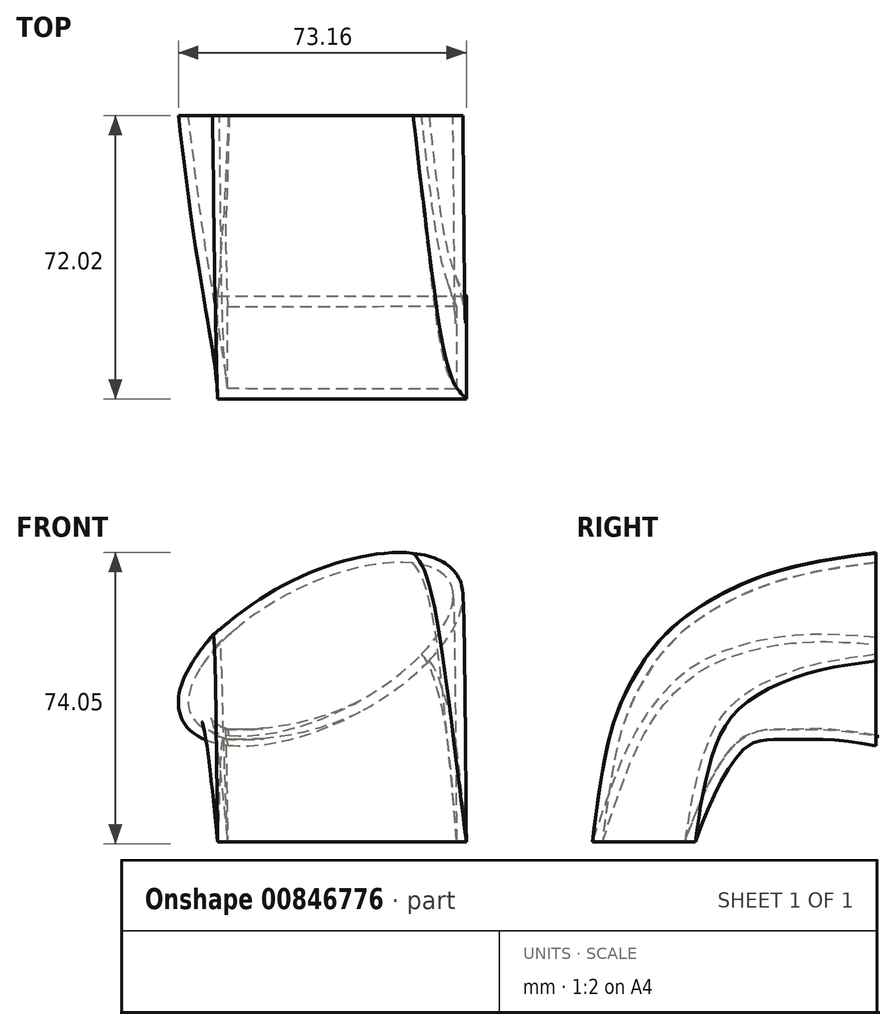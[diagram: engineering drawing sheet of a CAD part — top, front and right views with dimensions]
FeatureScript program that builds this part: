
annotation { "Feature Type Name" : "Feature", "Feature Type Description" : "" }
export const myFeature = defineFeature(function(context is Context, id is Id, definition is map)
    precondition{}
    {
        {
            var Q0;
            Q0=qCreatedBy(makeId("Front.planeOp"),FACE);
            var sketch = newSketch(context, id + "F0", { "sketchPlane" : qUnion([Q0])});
            skEllipse(sketch, "E0", {"center": v(10.24, 48.9) * mm, "majorRadius": 39.48 * mm, "minorRadius": 18.75 * mm, "majorAxis": v(0.89, 0.46)});
            skSolve(sketch);
        }
        {
            var Q0;
            Q0=qCreatedBy(makeId("Top.planeOp"),FACE);
            var sketch = newSketch(context, id + "F1", { "sketchPlane" : qUnion([Q0])});
            skLineSegment(sketch, "E1.bottom", {"start": v(-15.92, -72.02) * mm, "end": v(47.26, -72.02) * mm});
            skLineSegment(sketch, "E1.top", {"start": v(-15.92, -45.87) * mm, "end": v(47.26, -45.87) * mm});
            skLineSegment(sketch, "E1.left", {"start": v(-15.92, -72.02) * mm, "end": v(-15.92, -45.87) * mm});
            skLineSegment(sketch, "E1.right", {"start": v(47.26, -72.02) * mm, "end": v(47.26, -45.87) * mm});
            skSolve(sketch);
        }
        {
            var Q0;
            Q0=qCreatedBy(makeId("Right.planeOp"),FACE);
            var sketch = newSketch(context, id + "F2", { "sketchPlane" : qUnion([Q0])});
            skFitSpline(sketch, "E2", {"points": [v(0, 64.7) * mm, v(-52.1, 48.06) * mm, v(-72.02, 0) * mm], "startDerivative": vector(-116.53, -0.97) * mm, "endDerivative": vector(-23.25, -117.25) * mm});
            skSolve(sketch);
        }
        {
            var Q0;
            Q0=sQuery(id+"F2.wireOp",EDGE,"E2");
            var Q1;
            Q1=makeQuery(id+"F0.imprint","IMPRINT",FACE,{"disambiguationData":[TD([[makeQuery(id+"F0.imprint","IMPRINT",EDGE,{"derivedFrom":sQuery(id+"F0.wireOp",EDGE,"E0")}),1.0]])]});
            var Q2;
            Q2=makeQuery(id+"F1.imprint","IMPRINT",FACE,{"disambiguationData":[TD([[makeQuery(id+"F1.imprint","IMPRINT",EDGE,{"derivedFrom":sQuery(id+"F1.wireOp",EDGE,"E1.bottom")}),1.0]])]});
            loft(context, id + "F3", {"addSections" : true, "spine" : qUnion([Q0]), "sectionCount" : 5, "sheetProfilesArray" : [{ "sheetProfileEntities" : qUnion([Q1]) }, { "sheetProfileEntities" : qUnion([Q2]) }]});
        }
        {
            var Q0;
            Q0=makeQuery(id+"F3.opLoft","CAP_FACE",FACE,{"disambiguationData":[OSD([makeQuery(id+"F1.imprint","IMPRINT",FACE,{"disambiguationData":[TD([[makeQuery(id+"F1.imprint","IMPRINT",EDGE,{"derivedFrom":sQuery(id+"F1.wireOp",EDGE,"E1.bottom")}),1.0]])]})])],"isStart":true});
            var Q1;
            Q1=makeQuery(id+"F3.opLoft","CAP_FACE",FACE,{"disambiguationData":[OSD([makeQuery(id+"F0.imprint","IMPRINT",FACE,{"disambiguationData":[TD([[makeQuery(id+"F0.imprint","IMPRINT",EDGE,{"derivedFrom":sQuery(id+"F0.wireOp",EDGE,"E0")}),1.0]])]})])],"isStart":true});
            shell(context, id + "F4", {"entities" : qUnion([Q0, Q1]), "thickness" : 2.5 * mm});
        }
    });
